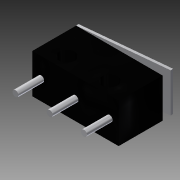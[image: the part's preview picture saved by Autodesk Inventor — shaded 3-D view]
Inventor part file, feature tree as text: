
AUTODESK INVENTOR PART (.ipt)
format: ipt  version: 2013 (Build 170138000, 138)  size: 114,176 bytes
history: native  units: mm
features: extrude x4, sketch x4
ambient origin geometry x8: Origin, YZ Plane, XZ Plane, XY Plane, X Axis, Y Axis, Z Axis, Center Point
bodies: Solid1 (feature_tree)
feature tree (8):
  extrude  "Extrusion1"  Depth=6.5278mm
  extrude  "Extrusion2"  Depth=0.381mm
  extrude  "Extrusion3"  Depth=5.8mm TaperAngle=0.0deg
  extrude  "Extrusion4"  Depth=0.889mm
  sketch  "Sketch1"  dims[d0=12.827mm d2=6.5278mm]
  sketch  "Sketch2"  dims[d3=5.8mm d4=0.0mm d5=0.381mm]
  sketch  "Sketch3"  dims[d7=1.27mm d8=5.8mm d9=0.0mm]
  sketch  "Sketch4"  dims[d10=10.16mm d12=0.889mm d13=3.81mm d14=0.0mm d15=6.35mm d17=1.905mm d18=2.286mm d19=3.81mm d20=0.0mm]
